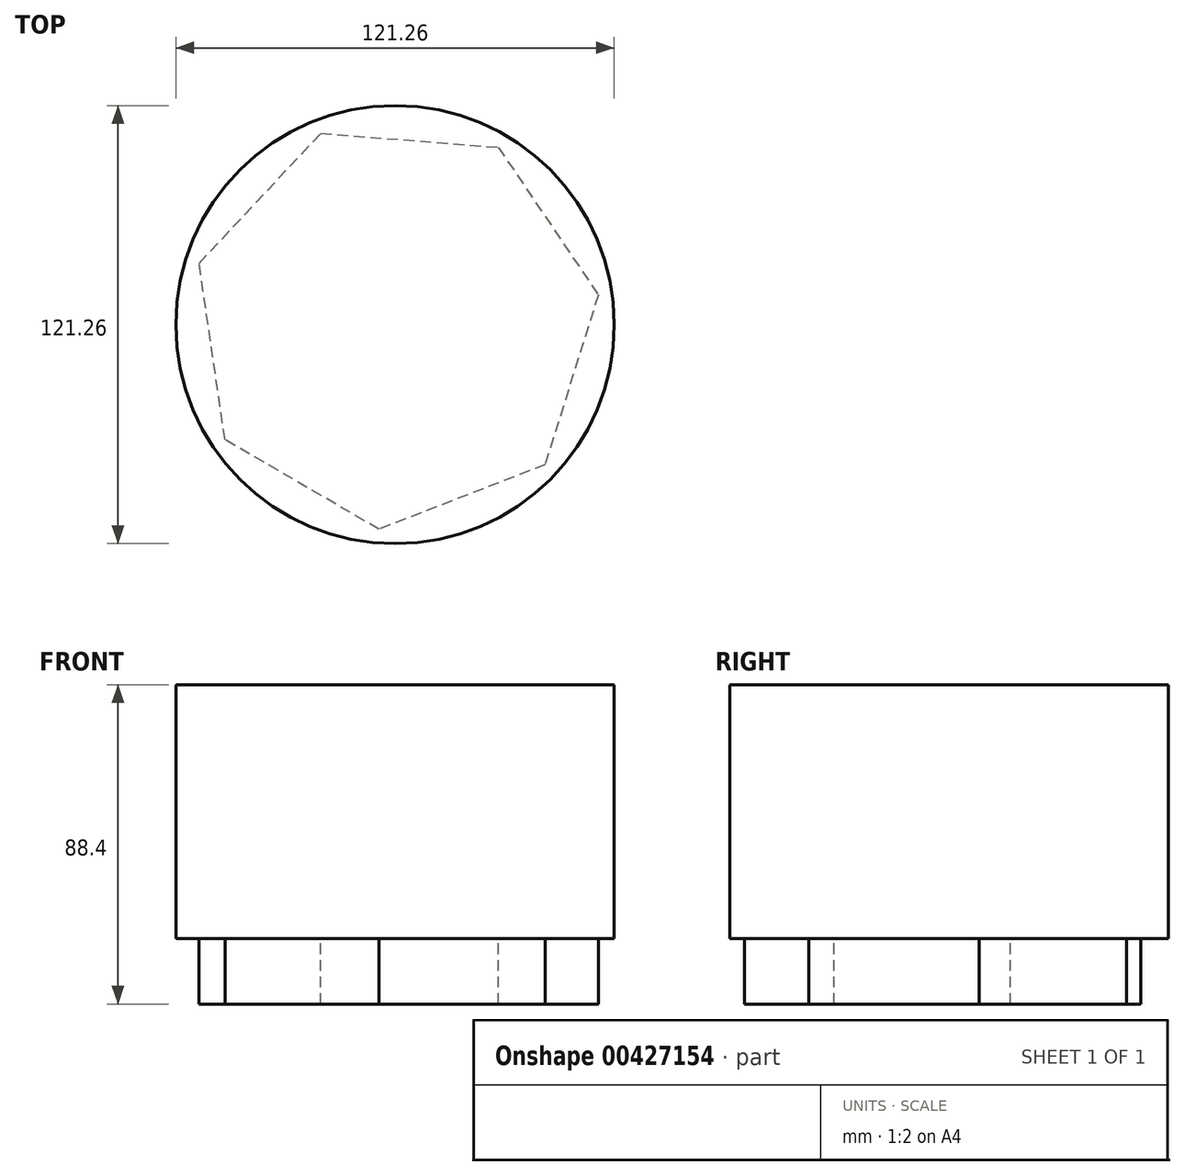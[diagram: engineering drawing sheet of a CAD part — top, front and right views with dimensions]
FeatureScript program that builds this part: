
annotation { "Feature Type Name" : "Feature", "Feature Type Description" : "" }
export const myFeature = defineFeature(function(context is Context, id is Id, definition is map)
    precondition{}
    {
        {
            var Q0;
            Q0=qCreatedBy(makeId("Top.planeOp"),FACE);
            var sketch = newSketch(context, id + "F0", { "sketchPlane" : qUnion([Q0])});
            skCircle(sketch, "E0", {"center": v(0, 0) * mm, "radius": 60.63 * mm});
            skSolve(sketch);
        }
        {
            var Q0;
            Q0=makeQuery(id+"F0.imprint","IMPRINT",FACE,{"disambiguationData":[TD([[makeQuery(id+"F0.imprint","IMPRINT",EDGE,{"derivedFrom":sQuery(id+"F0.wireOp",EDGE,"E0")}),1.0]])]});
            var sketch = newSketch(context, id + "F1", { "sketchPlane" : qUnion([Q0])});
            skCircle(sketch, "E1.cCircle", {"center": v(0, 0) * mm, "radius": 51.17 * mm, "construction": true});
            skLineSegment(sketch, "E1.0", {"start": v(-54.2, 16.94) * mm, "end": v(-20.55, 52.94) * mm});
            skLineSegment(sketch, "E1.1", {"start": v(-20.55, 52.94) * mm, "end": v(28.58, 49.08) * mm});
            skLineSegment(sketch, "E1.2", {"start": v(28.58, 49.08) * mm, "end": v(56.19, 8.26) * mm});
            skLineSegment(sketch, "E1.3", {"start": v(56.19, 8.26) * mm, "end": v(41.49, -38.78) * mm});
            skLineSegment(sketch, "E1.4", {"start": v(41.49, -38.78) * mm, "end": v(-4.45, -56.62) * mm});
            skLineSegment(sketch, "E1.5", {"start": v(-4.45, -56.62) * mm, "end": v(-47.04, -31.82) * mm});
            skLineSegment(sketch, "E1.6", {"start": v(-47.04, -31.82) * mm, "end": v(-54.2, 16.94) * mm});
            skPoint(sketch, "E1.0.midPoint", {"position": v(-37.38, 34.94) * mm});
            skSolve(sketch);
        }
        {
            var Q0;
            Q0=makeQuery(id+"F0.imprint","IMPRINT",FACE,{"disambiguationData":[TD([[makeQuery(id+"F0.imprint","IMPRINT",EDGE,{"derivedFrom":sQuery(id+"F0.wireOp",EDGE,"E0")}),1.0]])]});
            extrude(context, id + "F2", {"entities" : qUnion([Q0]), "depth" : 70.27 * mm});
        }
        {
            var Q0;
            Q0=makeQuery(id+"F1.imprint","IMPRINT",FACE,{"disambiguationData":[TD([[makeQuery(id+"F1.imprint","IMPRINT",EDGE,{"derivedFrom":sQuery(id+"F1.wireOp",EDGE,"E1.0")}),-1.0]])]});
            extrude(context, id + "F3", {"entities" : qUnion([Q0]), "operationType" : NewBodyOperationType.ADD, "oppositeDirection" : true, "depth" : 18.13 * mm});
        }
    });
